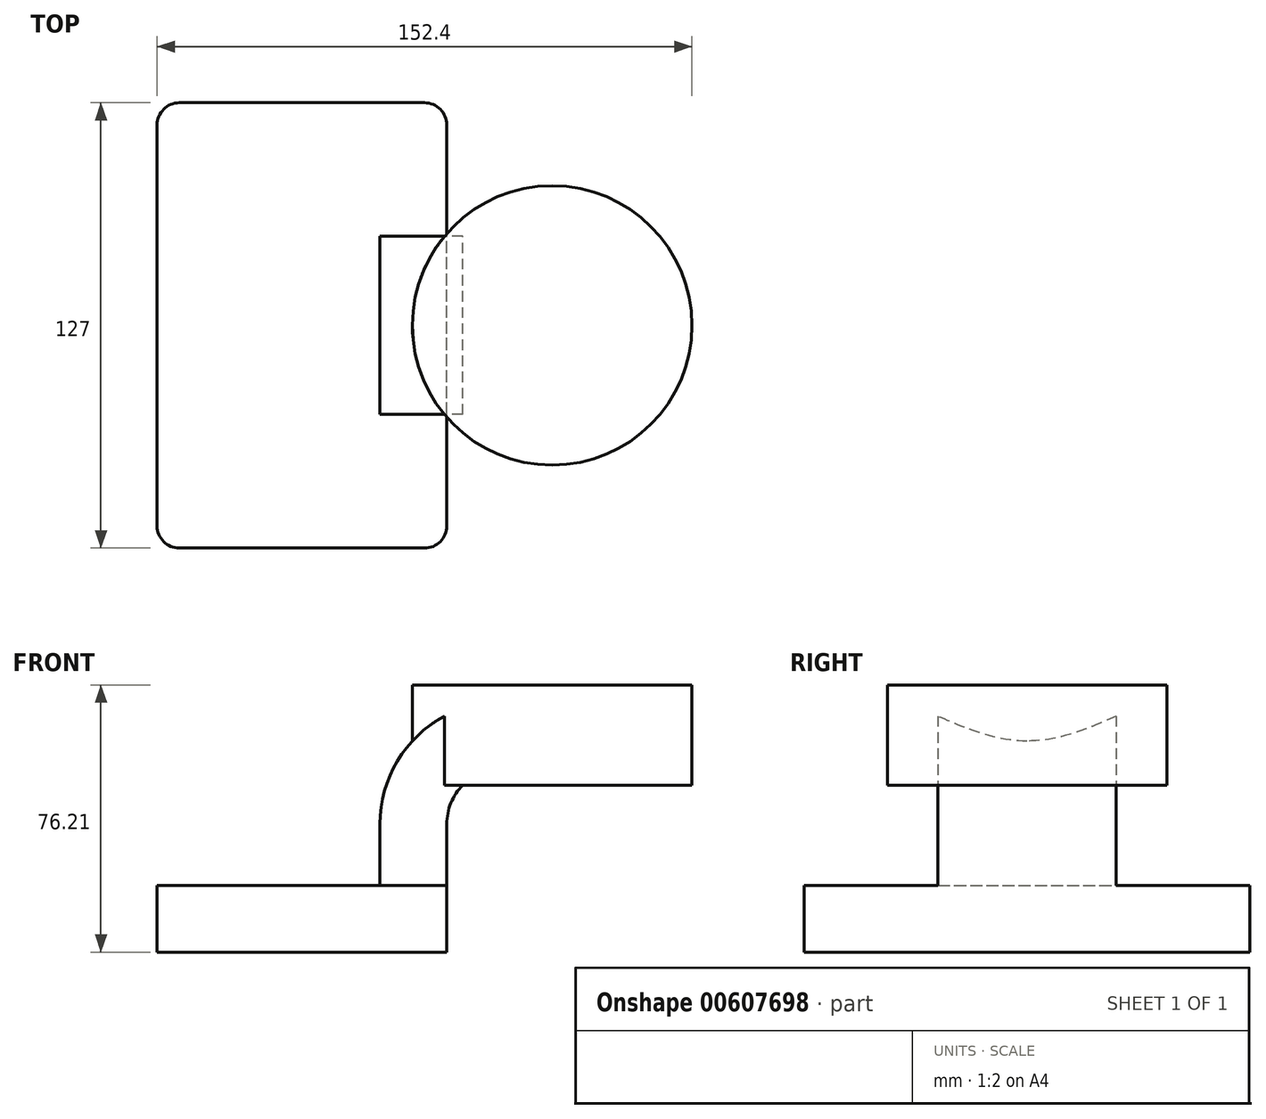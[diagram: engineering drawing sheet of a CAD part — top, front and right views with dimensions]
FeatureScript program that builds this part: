
annotation { "Feature Type Name" : "Feature", "Feature Type Description" : "" }
export const myFeature = defineFeature(function(context is Context, id is Id, definition is map)
    precondition{}
    {
        {
            var Q0;
            Q0=qCreatedBy(makeId("Front.planeOp"),FACE);
            var sketch = newSketch(context, id + "F0", { "sketchPlane" : qUnion([Q0])});
            skLineSegment(sketch, "E0.bottom", {"start": v(41.28, 9.52) * mm, "end": v(-41.28, 9.52) * mm});
            skLineSegment(sketch, "E0.top", {"start": v(41.28, -9.53) * mm, "end": v(-41.27, -9.53) * mm});
            skLineSegment(sketch, "E0.left", {"start": v(41.28, 9.52) * mm, "end": v(41.28, -9.53) * mm});
            skLineSegment(sketch, "E0.right", {"start": v(-41.28, 9.52) * mm, "end": v(-41.28, -9.53) * mm});
            skPoint(sketch, "E0.middle", {"position": v(0, 0) * mm});
            skLineSegment(sketch, "E1.bottom", {"start": v(111.12, 66.68) * mm, "end": v(60.32, 66.68) * mm});
            skLineSegment(sketch, "E1.top", {"start": v(111.12, 38.1) * mm, "end": v(60.32, 38.1) * mm});
            skLineSegment(sketch, "E1.left", {"start": v(111.12, 66.68) * mm, "end": v(111.12, 38.1) * mm});
            skLineSegment(sketch, "E1.right", {"start": v(60.32, 66.68) * mm, "end": v(60.32, 38.1) * mm});
            skPoint(sketch, "E1.middle", {"position": v(85.72, 52.39) * mm});
            skLineSegment(sketch, "E2", {"start": v(41.28, 9.52) * mm, "end": v(41.28, 27) * mm});
            skArc(sketch, "E3", {"start": v(41.27, 27) * mm, "mid": v(45.92, 38.23) * mm, "end": v(57.15, 42.88) * mm});
            skLineSegment(sketch, "E4", {"start": v(57.15, 42.88) * mm, "end": v(71.3, 42.88) * mm});
            skLineSegment(sketch, "E5.0", {"start": v(57.15, 61.93) * mm, "end": v(71.3, 61.93) * mm});
            skArc(sketch, "E5.1", {"start": v(22.22, 27) * mm, "mid": v(32.45, 51.7) * mm, "end": v(57.15, 61.93) * mm});
            skLineSegment(sketch, "E5.2", {"start": v(22.22, 9.52) * mm, "end": v(22.22, 27) * mm});
            skLineSegment(sketch, "E6", {"start": v(71.3, 38.1) * mm, "end": v(71.3, 66.68) * mm});
            skFitSpline(sketch, "E7", {"points": [v(-41.27, 9.52) * mm, v(57.15, 61.93) * mm], "startDerivative": vector(14.54, 100.58) * mm, "endDerivative": vector(206.68, -15.61) * mm});
            skSolve(sketch);
        }
        {
            var Q0;
            Q0=makeQuery(id+"F0.imprint","IMPRINT",FACE,{"disambiguationData":[TD([[makeQuery(id+"F0.imprint","IMPRINT",EDGE,{"derivedFrom":sQuery(id+"F0.wireOp",EDGE,"E0.top")}),-1.0]])]});
            extrude(context, id + "F1", {"entities" : qUnion([Q0]), "endBound" : BoundingType.SYMMETRIC, "depth" : 127 * mm, "offsetDistance" : 25.4 * mm});
        }
        {
            var Q0;
            {var subQ1=sQuery(id+"F0.wireOp",EDGE,"E2");Q0=makeQuery(id+"F0.imprint","IMPRINT",FACE,{"disambiguationData":[TD([[makeQuery(id+"F0.imprint","IMPRINT",EDGE,{"derivedFrom":subQ1}),1.0]])]});}
            var Q1;
            {var subQ0=sQuery(id+"F0.wireOp",EDGE,"E5.0");var subQ1=sQuery(id+"F0.wireOp",EDGE,"E1.right");var subQ2=makeQuery(id+"F0.imprint","INTERSECT",VERTEX,{"derivedFrom":[subQ1,subQ0]});Q1=makeQuery(id+"F0.imprint","IMPRINT",FACE,{"disambiguationData":[TD([[makeQuery(id+"F0.imprint","IMPRINT",EDGE,{"disambiguationData":[TD([[subQ2,-1.0]])],"derivedFrom":subQ1}),1.0]])]});}
            extrude(context, id + "F2", {"entities" : qUnion([Q0, Q1]), "operationType" : NewBodyOperationType.ADD, "endBound" : BoundingType.SYMMETRIC, "depth" : 50.8 * mm, "offsetDistance" : 25.4 * mm});
        }
        {
            var Q0;
            Q0=makeQuery(id+"F0.imprint","IMPRINT",FACE,{"disambiguationData":[TD([[makeQuery(id+"F0.imprint","IMPRINT",EDGE,{"derivedFrom":sQuery(id+"F0.wireOp",EDGE,"E5.1")}),1.0]])]});
            extrude(context, id + "F3", {"entities" : qUnion([Q0]), "operationType" : NewBodyOperationType.ADD, "endBound" : BoundingType.SYMMETRIC, "depth" : 15.88 * mm, "offsetDistance" : 25.4 * mm});
        }
        {
            var Q0;
            {var subQ4=sQuery(id+"F0.wireOp",EDGE,"E1.left");Q0=makeQuery(id+"F0.imprint","IMPRINT",FACE,{"disambiguationData":[TD([[makeQuery(id+"F0.imprint","IMPRINT",EDGE,{"derivedFrom":subQ4}),-1.0]])]});}
            var Q1;
            Q1=sQuery(id+"F0.wireOp",EDGE,"E6");
            revolve(context, id + "F4", {"operationType" : NewBodyOperationType.ADD, "entities" : qUnion([Q0]), "axis" : qUnion([Q1]), "revolveType" : RevolveType.FULL});
        }
        {
            var Q0;
            Q0=makeQuery(id+"F1.opExtrude","CAP_EDGE",EDGE,{"disambiguationData":[OSD([sQuery(id+"F0.wireOp",EDGE,"E0.right")])],"isStart":false});
            var Q1;
            Q1=makeQuery(id+"F1.opExtrude","CAP_EDGE",EDGE,{"disambiguationData":[OSD([sQuery(id+"F0.wireOp",EDGE,"E0.right")])],"isStart":true});
            var Q2;
            Q2=makeQuery(id+"F1.opExtrude","CAP_EDGE",EDGE,{"disambiguationData":[OSD([sQuery(id+"F0.wireOp",EDGE,"E0.left")])],"isStart":false});
            var Q3;
            Q3=makeQuery(id+"F1.opExtrude","CAP_EDGE",EDGE,{"disambiguationData":[OSD([sQuery(id+"F0.wireOp",EDGE,"E0.left")])],"isStart":true});
            fillet(context, id + "F5", {"entities" : qUnion([Q0, Q1, Q2, Q3]), "radius" : 6.35 * mm, "tangentPropagation" : true, "allowEdgeOverflow" : false});
        }
    });
